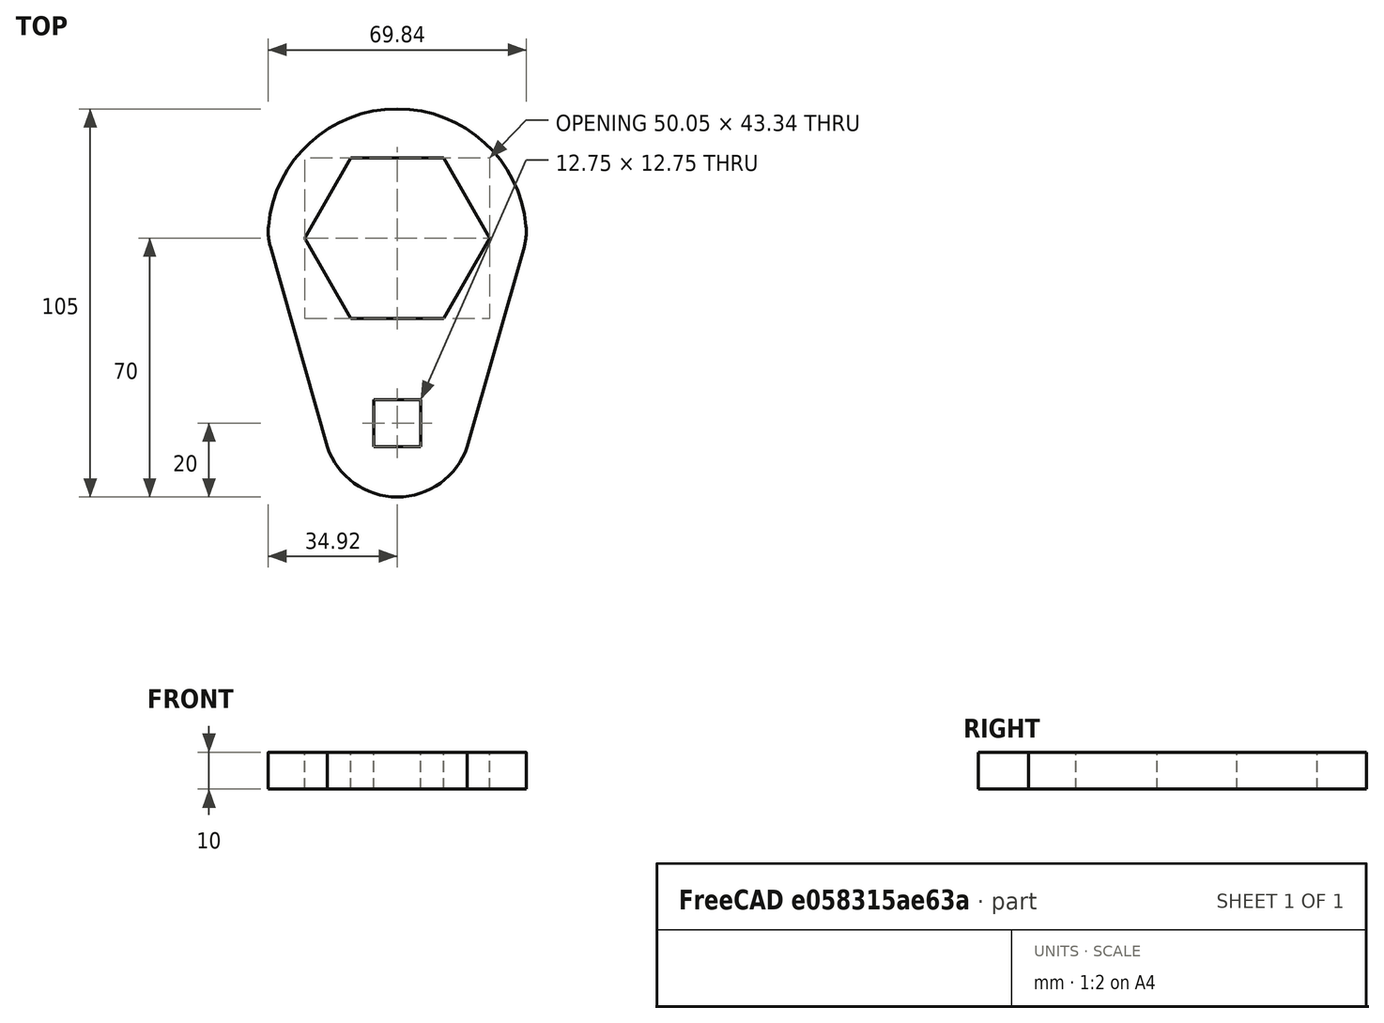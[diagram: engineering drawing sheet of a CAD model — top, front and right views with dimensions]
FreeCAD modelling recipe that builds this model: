
FCSTD DOCUMENT  (FreeCAD 0.18R16131 (Git))
Label: transmission wrench 50 13 w fea
License: All rights reserved
LicenseURL: http://en.wikipedia.org/wiki/All_rights_reserved
objects: Fem::FemMeshObjectPython×2, Sketcher::SketchObject×1, PartDesign::Pad×1, PartDesign::Fillet×1, PartDesign::Body×1, Fem::FemSolverObjectPython×1, App::MaterialObjectPython×1, Fem::ConstraintFixed×1, Fem::ConstraintForce×1, Fem::FemResultObjectPython×1, Fem::FemAnalysis×1
note: 5 computed .brp shape members not serialized (recipe doc carries the construction recipe); baked Part::Feature solids carry a one-line shape summary decoded from their .brp

FEATURE [Sketcher::SketchObject] Sketch
  MapMode = 5
  Support = -> [XY_Plane]
  expr: Constraints[29] = 25.4 * 0.5 + 0.05
  sketch-geometry (17):
    g0: LineSegment StartX=-25.025 StartY=0 StartZ=0 EndX=-12.5125 EndY=-21.6723 EndZ=0
    g1: LineSegment StartX=-12.5125 StartY=-21.6723 StartZ=0 EndX=12.5125 EndY=-21.6723 EndZ=0
    g2: LineSegment StartX=12.5125 StartY=-21.6723 StartZ=0 EndX=25.025 EndY=0 EndZ=0
    g3: LineSegment StartX=25.025 StartY=0 StartZ=0 EndX=12.5125 EndY=21.6723 EndZ=0
    g4: LineSegment StartX=12.5125 StartY=21.6723 StartZ=0 EndX=-12.5125 EndY=21.6723 EndZ=0
    g5: LineSegment StartX=-12.5125 StartY=21.6723 StartZ=0 EndX=-25.025 EndY=0 EndZ=0
    g6: Circle [constr] CenterX=0 CenterY=0 CenterZ=0 NormalX=0 NormalY=0 NormalZ=1 AngleXU=0 Radius=25.025
    g7: LineSegment StartX=6.375 StartY=-56.375 StartZ=0 EndX=6.375 EndY=-43.625 EndZ=0
    g8: LineSegment StartX=6.375 StartY=-43.625 StartZ=0 EndX=-6.375 EndY=-43.625 EndZ=0
    g9: LineSegment StartX=-6.375 StartY=-43.625 StartZ=0 EndX=-6.375 EndY=-56.375 EndZ=0
    g10: LineSegment StartX=-6.375 StartY=-56.375 StartZ=0 EndX=6.375 EndY=-56.375 EndZ=0
    g11: Circle [constr] CenterX=0 CenterY=-50 CenterZ=0 NormalX=0 NormalY=0 NormalZ=1 AngleXU=0 Radius=9.01561
    g12: ArcOfCircle CenterX=0 CenterY=0 CenterZ=0 NormalX=0 NormalY=0 NormalZ=1 AngleXU=0 Radius=35 StartAngle=0 EndAngle=3.14159
    g13: ArcOfCircle CenterX=0 CenterY=-50 CenterZ=0 NormalX=0 NormalY=0 NormalZ=1 AngleXU=0 Radius=20 StartAngle=3.466 EndAngle=5.95877
    g14: LineSegment StartX=-35 StartY=4.3e-15 StartZ=0 EndX=-18.9568 EndY=-56.375 EndZ=0
    g15: LineSegment StartX=18.9568 StartY=-56.375 StartZ=0 EndX=35 EndY=0 EndZ=0
    g16: LineSegment [constr] StartX=-18.9568 StartY=-56.375 StartZ=0 EndX=18.9568 EndY=-56.375 EndZ=0
  constraints (44):
    c: Coincident(g0,g1)
    c: Coincident(g1,g2)
    c: Coincident(g2,g3)
    c: Coincident(g3,g4)
    c: Coincident(g4,g5)
    c: Coincident(g5,g0)
    c: Equal(g0, g1-g5) x5
    c: PointOnObject(g0,g6)
    c: PointOnObject(g1,g6)
    c: PointOnObject(g2,g6)
    c: PointOnObject(g3,g6)
    c: Symmetric(g0,g2,g-1)
    c: Coincident(g7,g8)
    c: Coincident(g8,g9)
    c: Coincident(g9,g10)
    c: Coincident(g10,g7)
    c: Equal(g7,g8)
    c: Equal(g7,g9)
    c: Equal(g7,g10)
    c: PointOnObject(g7,g11)
    c: PointOnObject(g8,g11)
    c: PointOnObject(g9,g11)
    c: PointOnObject(g10,g11)
    c: PointOnObject(g11,g-2)
    c: Parallel(g8,g-1)
    c: DistanceX(g9,g7) = 12.75
    c: DistanceY(g11,g-1) = 50
    c: PointOnObject(g12,g-1)
    c: PointOnObject(g12,g-1)
    c: Coincident(g14,g12)
    c: Coincident(g15,g12)
    c: Coincident(g12,g-1)
    c: Radius(g12) = 35
    c: Radius(g13) = 20
    c: Coincident(g15,g13)
    c: Coincident(g13,g14)
    c: Coincident(g13,g11)
    c: Coincident(g13,g16)
    c: Coincident(g16,g13)
    c: Parallel(g16,g-1)
    c: PointOnObject(g7,g16)
    c: Coincident(g6,g12)
    c: PointOnObject(g0,g-1)
    c: DistanceX(g0,g2) = 50.05
FEATURE [PartDesign::Pad] Pad
  Length = 10
  Length2 = 100
  Profile = -> Sketch
  Type = 0
FEATURE [PartDesign::Fillet] Fillet
  Base = -> Pad [Edge2,Edge5,Edge8,Edge1]
  BaseFeature = -> Pad
  Radius = 15
FEATURE [PartDesign::Body] Body
  Group = -> [Sketch,Pad,Fillet]
  Origin = -> Origin
  Tip = -> Fillet
FEATURE [Fem::FemSolverObjectPython] CalculiXccxTools  # FEM object (typed FeaturePython)
  AnalysisType = 0
  BeamShellResultOutput3D = false
  EigenmodeHighLimit = 1000000
  EigenmodeLowLimit = 0
  EigenmodesCount = 10
  GeometricalNonlinearity = 0
  IterationsControlParameterCutb = 0.25,0.5,0.75,0.85,,,1.5,
  IterationsControlParameterIter = 4,8,9,200,10,400,,200,,
  IterationsControlParameterTimeUse = false
  IterationsThermoMechMaximum = 200
  IterationsUserDefinedIncrementations = false
  IterationsUserDefinedTimeStepLength = false
  MaterialNonlinearity = 0
  MatrixSolverType = 0
  SplitInputWriter = false
  ThermoMechSteadyState = true
  TimeEnd = 1
  TimeInitialStep = 1
FEATURE [Fem::FemMeshObjectPython] FEMMeshGmsh  # FEM object (typed FeaturePython)
  Algorithm2D = 0
  Algorithm3D = 0
  CharacteristicLengthMax = 0
  CharacteristicLengthMin = 0
  CoherenceMesh = true
  ElementDimension = 0
  ElementOrder = 1
  GeometryTolerance = 1e-06
  GroupsOfNodes = false
  HighOrderOptimize = false
  OptimizeNetgen = false
  OptimizeStd = true
  Part = -> Fillet
  RecombineAll = false
FEATURE [App::MaterialObjectPython] SolidMaterial  # material (typed FeaturePython)
  Category = 0
  Material = Density=7900 kg/m^3,Description=Standard steel material for CalculiX sample calculations,Father=Metal,Name=CalculiX-Steel,PoissonRatio=0.3,+4 more (map truncated)
FEATURE [Fem::ConstraintFixed] FemConstraintFixed
  NormalDirection = (0.866025,0.5,0)
  Normals = (72) [(0.866025,0.5,0),(0.866025,0.5,0),(0.866025,0.5,0),(0.866025,0.5,0),(0.866025,0.5,0),(0.866025,0.5,0),(0.866025,0.5,0),(0.866025,0.5,0),+64 more]
  Points = (72) [(-25.025,0,10),(-20.8542,-7.2241,10),(-16.6833,-14.4482,10),(-12.5125,-21.6723,10),(-25.025,0,5),(-20.8542,-7.2241,5),(-16.6833,-14.4482,5),+65 more]
  References = -> [Fillet]
FEATURE [Fem::ConstraintForce] FemConstraintForce
  DirectionVector = (-1,-1e-16,0)
  Force = 8300
  NormalDirection = (1,1e-16,0)
  Points = (9) [(-6.375,-43.625,10),(-6.375,-50,10),(-6.375,-56.375,10),(-6.375,-43.625,5),(-6.375,-50,5),(-6.375,-56.375,5),(-6.375,-43.625,0),(-6.375,-50,0),+1 more]
  References = -> [Fillet]
  Reversed = true
FEATURE [Fem::FemMeshObjectPython] Result_mesh  # FEM object (typed FeaturePython)
FEATURE [Fem::FemResultObjectPython] CalculiX_static_results  # FEM object (typed FeaturePython)
  DisplacementLengths = [0.00044892,0.000556154,0.000445543,0.000560269,0.00059088,0.000735416,0.0143415,0.0178228,0,0,0,0,0,0,0.0178296,0.0147793,0.00952303,0.00686415,0.000589477,0.000737086,0.0143082,0.0177381,0,0,0,0,0,0,0.0179031,0.0147263,0.00947894,+767 more]
  DisplacementVectors = (798) [(-3.81665e-05,-0.000446248,3.05742e-05),(-4.53295e-05,0.000552914,-3.92301e-05),(-3.70703e-05,-0.000442689,-3.40748e-05),+795 more]
  Eigenmode = 0
  EigenmodeFrequency = 0
  MaxShear = [2.56281,3.08355,2.42239,3.20469,3.08287,3.82907,7.04097,23.089,0.758954,7.95793,0.63049,6.34987,21.273,21.3519,20.9698,24.1335,49.2228,17.7604,2.9542,3.63783,8.88485,19.8499,0.776975,7.81554,0.642161,6.23905,20.813,21.2283,25.3282,24.2372,+768 more]
  Mesh = -> Result_mesh
  NodeNumbers = [1,2,3,4,5,6,7,8,9,10,11,12,13,14,15,16,17,18,19,20,21,22,23,24,25,26,27,28,29,30,31,32,33,34,35,36,37,38,39,40,41,42,43,44,45,46,47,48,49,50,51,52,53,54,55,56,57,58,59,60,61,62,63,64,65,66,67,68,69,+729 more]
  PrincipalMax = [4.93765,0.0506515,4.80956,0.26246,5.85966,0.38619,9.25445,43.6332,0.732832,6.53931,0.659796,7.53164,29.7466,16.5343,6.72486,51.0463,94.1369,-4.71651,5.66426,0.30886,12.5954,38.2505,0.712885,6.67375,0.669372,7.19733,23.3237,15.2511,1.83868,+769 more]
  PrincipalMed = [0.0429328,-0.0702873,0.0358098,-0.0305531,-0.172179,0.242351,0.0729102,3.37597,0.0416688,-0.707216,-0.0278116,0.592784,4.22698,-2.1213,-1.13691,8.28873,6.4898,-6.92531,-0.127569,0.152829,0.148048,2.09788,-0.0235986,-0.254585,0.00717042,+773 more]
  PrincipalMin = [-0.187976,-6.11644,-0.035224,-6.14693,-0.306068,-7.27196,-4.82749,-2.54487,-0.785076,-9.37656,-0.601185,-5.16811,-12.7993,-26.1695,-35.2148,2.77926,-4.30862,-40.2373,-0.244145,-6.9668,-5.17426,-1.44921,-0.841065,-8.95732,-0.614949,-5.28076,+772 more]
  ResultType = Fem::FemResultMechanical
  Stats = [-0.0180664,-0.00367904,8.52174e-05,-0.00467873,0.000162828,0.00591838,-0.000825619,3.82025e-06,0.000639316,0,0.00406593,0.0181882,0.0500579,21.2156,93.8652,-9.86986,11.7957,94.9362,-57.819,-0.219944,12.2252,-88.2095,-11.1558,6.29983,+15 more]
  StrainVectors = (798) [(-7.87895e-06,2.35944e-05,-6.58667e-06),(8.97193e-06,-2.89996e-05,8.33989e-06),(-7.02388e-06,2.28495e-05,-6.66346e-06),+795 more]
  StressValues = [5.01416,6.10752,4.80966,6.26802,6.09989,7.58725,12.3818,43.5207,1.31629,13.8019,1.09353,11.0141,37.0898,37.0807,38.6137,45.7618,93.5151,34.4695,5.85099,7.19892,15.796,38.0504,1.34637,13.5659,1.11244,10.8321,36.0824,36.8671,46.7377,46.4184,+768 more]
  StressVectors = (798) [(-0.166767,4.91739,0.0419857),(0.0332935,-6.10057,-0.0688038),(-0.0245922,4.80111,0.0336298),(0.237436,-6.12206,-0.0303953),+794 more]
  Time = 0
FEATURE [Fem::FemAnalysis] Analysis
  Group = -> [CalculiXccxTools,FEMMeshGmsh,SolidMaterial,FemConstraintFixed,FemConstraintForce,CalculiX_static_results]
